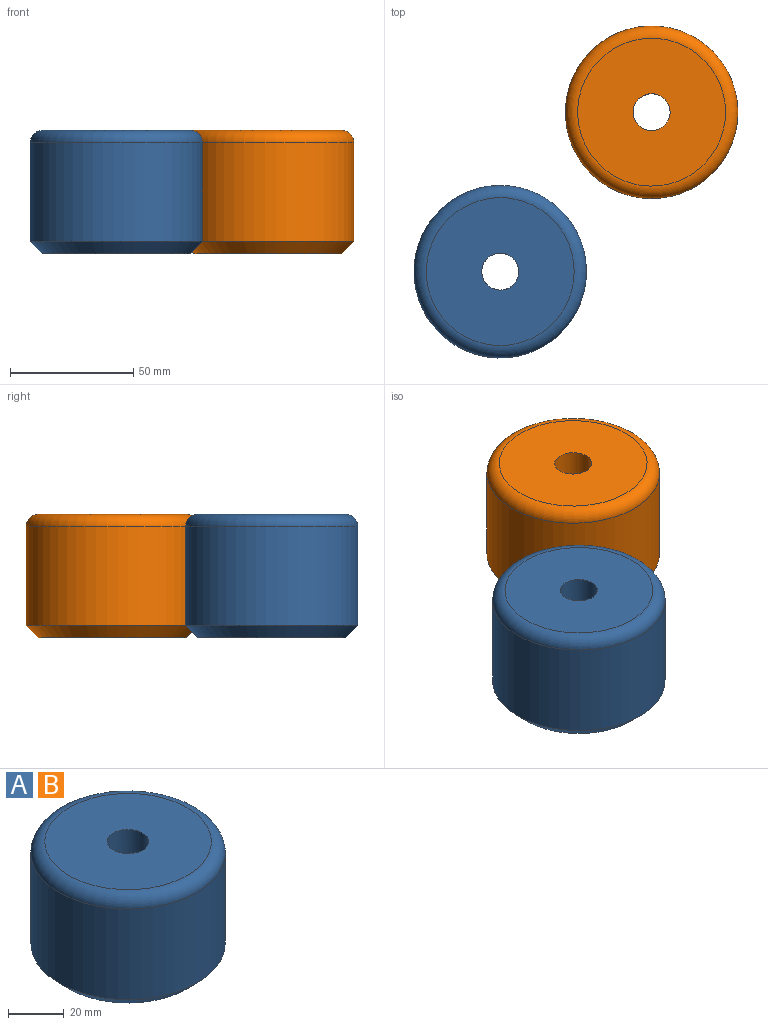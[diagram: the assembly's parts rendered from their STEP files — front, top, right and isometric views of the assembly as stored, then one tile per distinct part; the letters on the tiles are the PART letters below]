
ASSEMBLY  parts=2 mates=1
PART A: 8 faces, bbox 75.8x75.8x50 mm
  f0: cylinder r=35mm len=70mm, axis (0,0,1), area 8796.5mm2, adj f5,f6
  f1: plane 60x60mm, normal (0,0,-1), area 1570.8mm2, adj f3,f6
  f2: plane 60x60mm, normal (0,0,1), area 2650.7mm2, adj f5,f7
  f3: cylinder r=20mm len=40mm, axis (0,0,-1), area 3141.6mm2, adj f1,f4
  f4: plane 40x40mm, normal (0,0,-1), area 1079.9mm2, adj f3,f7
  f5: torus R=30mm, axis (0,0,1), area 1637.5mm2, adj f0,f2
  f6: cone r=35mm half-angle=45deg, axis (0,0,1), area 1443.9mm2, adj f0,f1
  f7: cylinder r=7.5mm len=25mm, axis (0,0,1), area 1178.1mm2, adj f2,f4
PART B: same geometry as A
PLACE A t=(-61.42,-64.69,3.75)mm
PLACE B t=(0,0,3.75)mm
MATE planar A.f0 <-> B.f0  axis (0,0,1) through (-61.42,-64.69,3.75)mm
